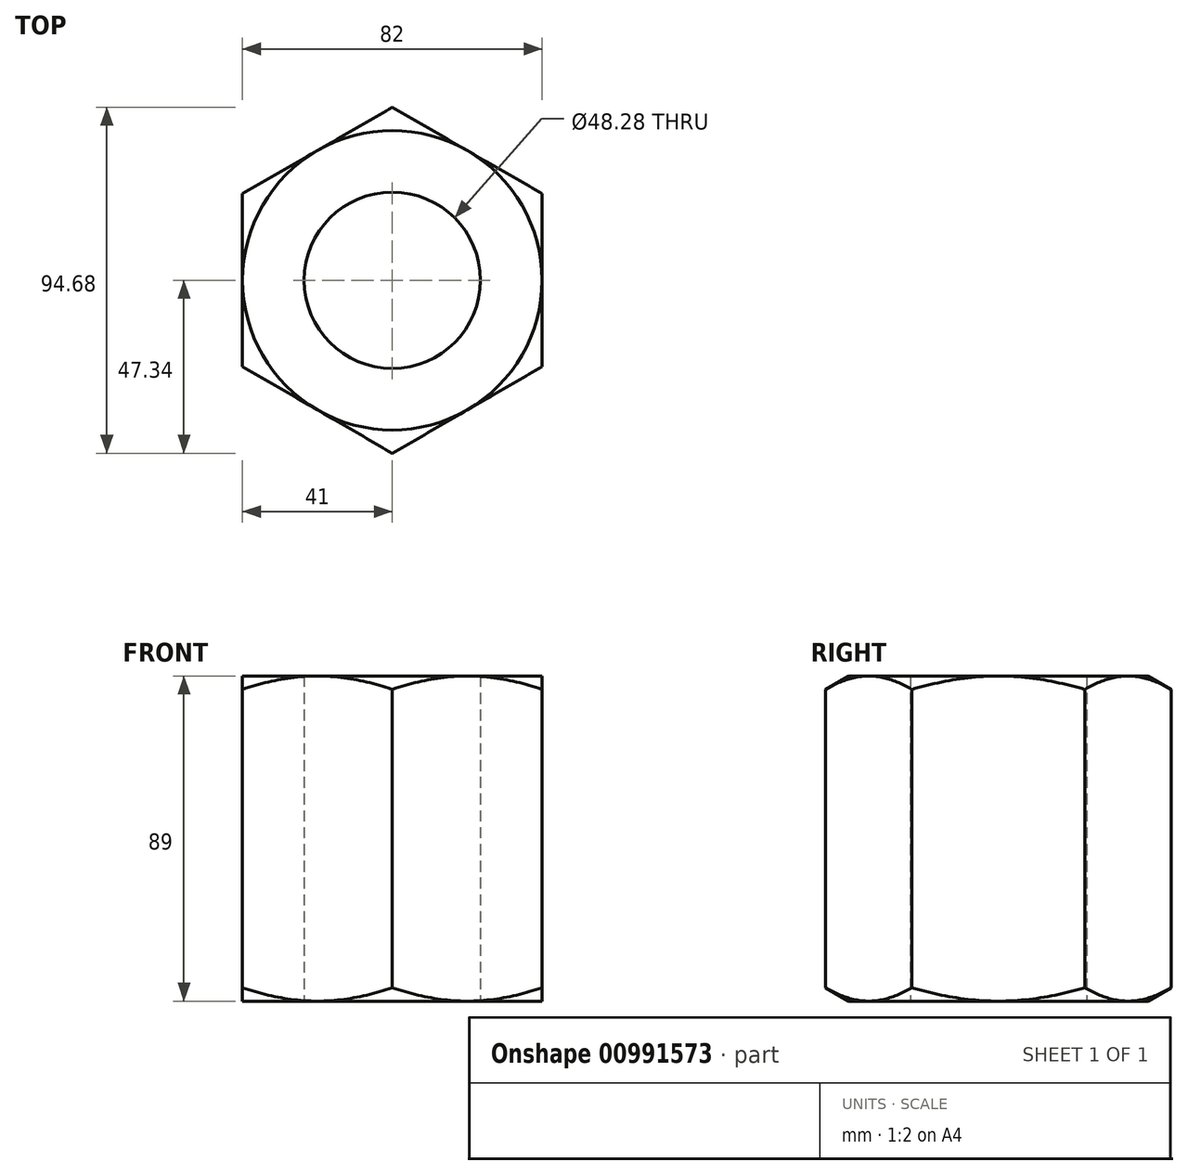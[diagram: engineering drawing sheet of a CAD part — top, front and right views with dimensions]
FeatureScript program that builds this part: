
annotation { "Feature Type Name" : "Feature", "Feature Type Description" : "" }
export const myFeature = defineFeature(function(context is Context, id is Id, definition is map)
    precondition{}
    {
        {
            var Q0;
            Q0=qCreatedBy(makeId("Top.planeOp"),FACE);
            var sketch = newSketch(context, id + "F0", { "sketchPlane" : qUnion([Q0])});
            skCircle(sketch, "E0.cCircle", {"center": v(0, 0) * mm, "radius": 41 * mm, "construction": true});
            skLineSegment(sketch, "E0.0", {"start": v(0, 47.34) * mm, "end": v(41, 23.67) * mm});
            skLineSegment(sketch, "E0.1", {"start": v(41, 23.67) * mm, "end": v(41, -23.67) * mm});
            skLineSegment(sketch, "E0.2", {"start": v(41, -23.67) * mm, "end": v(0, -47.34) * mm});
            skLineSegment(sketch, "E0.3", {"start": v(0, -47.34) * mm, "end": v(-41, -23.67) * mm});
            skLineSegment(sketch, "E0.4", {"start": v(-41, -23.67) * mm, "end": v(-41, 23.67) * mm});
            skLineSegment(sketch, "E0.5", {"start": v(-41, 23.67) * mm, "end": v(0, 47.34) * mm});
            skPoint(sketch, "E0.0.midPoint", {"position": v(20.5, 35.5) * mm});
            skCircle(sketch, "E1", {"center": v(0, 0) * mm, "radius": 24.14 * mm});
            skSolve(sketch);
        }
        {
            var Q0;
            Q0 = qSketchRegion(id + "F0", true);
            extrude(context, id + "F1", {"entities" : qUnion([Q0]), "depth" : 89 * mm, "offsetDistance" : 25 * mm});
        }
        {
            var Q0;
            Q0=qCreatedBy(makeId("Front.planeOp"),FACE);
            var sketch = newSketch(context, id + "F2", { "sketchPlane" : qUnion([Q0])});
            skLineSegment(sketch, "E2", {"start": v(0, 0) * mm, "end": v(0, 89) * mm, "construction": true});
            skLineSegment(sketch, "E3", {"start": v(0, 44.5) * mm, "end": v(41.31, 44.5) * mm, "construction": true});
            skLineSegment(sketch, "E4", {"start": v(82.78, 64.88) * mm, "end": v(82.78, 89) * mm});
            skLineSegment(sketch, "E5", {"start": v(82.78, 89) * mm, "end": v(41, 89) * mm});
            skLineSegment(sketch, "E6", {"start": v(41, 89) * mm, "end": v(82.78, 64.88) * mm});
            skLineSegment(sketch, "E7.MirrorCS", {"start": v(82.78, 0) * mm, "end": v(41, 0) * mm});
            skLineSegment(sketch, "E8.MirrorCS", {"start": v(41, 0) * mm, "end": v(82.78, 24.12) * mm});
            skLineSegment(sketch, "E9.MirrorCS", {"start": v(82.78, 24.12) * mm, "end": v(82.78, 0) * mm});
            skSolve(sketch);
        }
        {
            var Q0;
            Q0 = qSketchRegion(id + "F2", true);
            var Q1;
            Q1=sQuery(id+"F2.wireOp",EDGE,"E2");
            revolve(context, id + "F3", {"operationType" : NewBodyOperationType.REMOVE, "surfaceOperationType" : NewSurfaceOperationType.NEW, "entities" : qUnion([Q0]), "axis" : qUnion([Q1]), "revolveType" : RevolveType.FULL, "oppositeDirection" : true});
        }
    });
